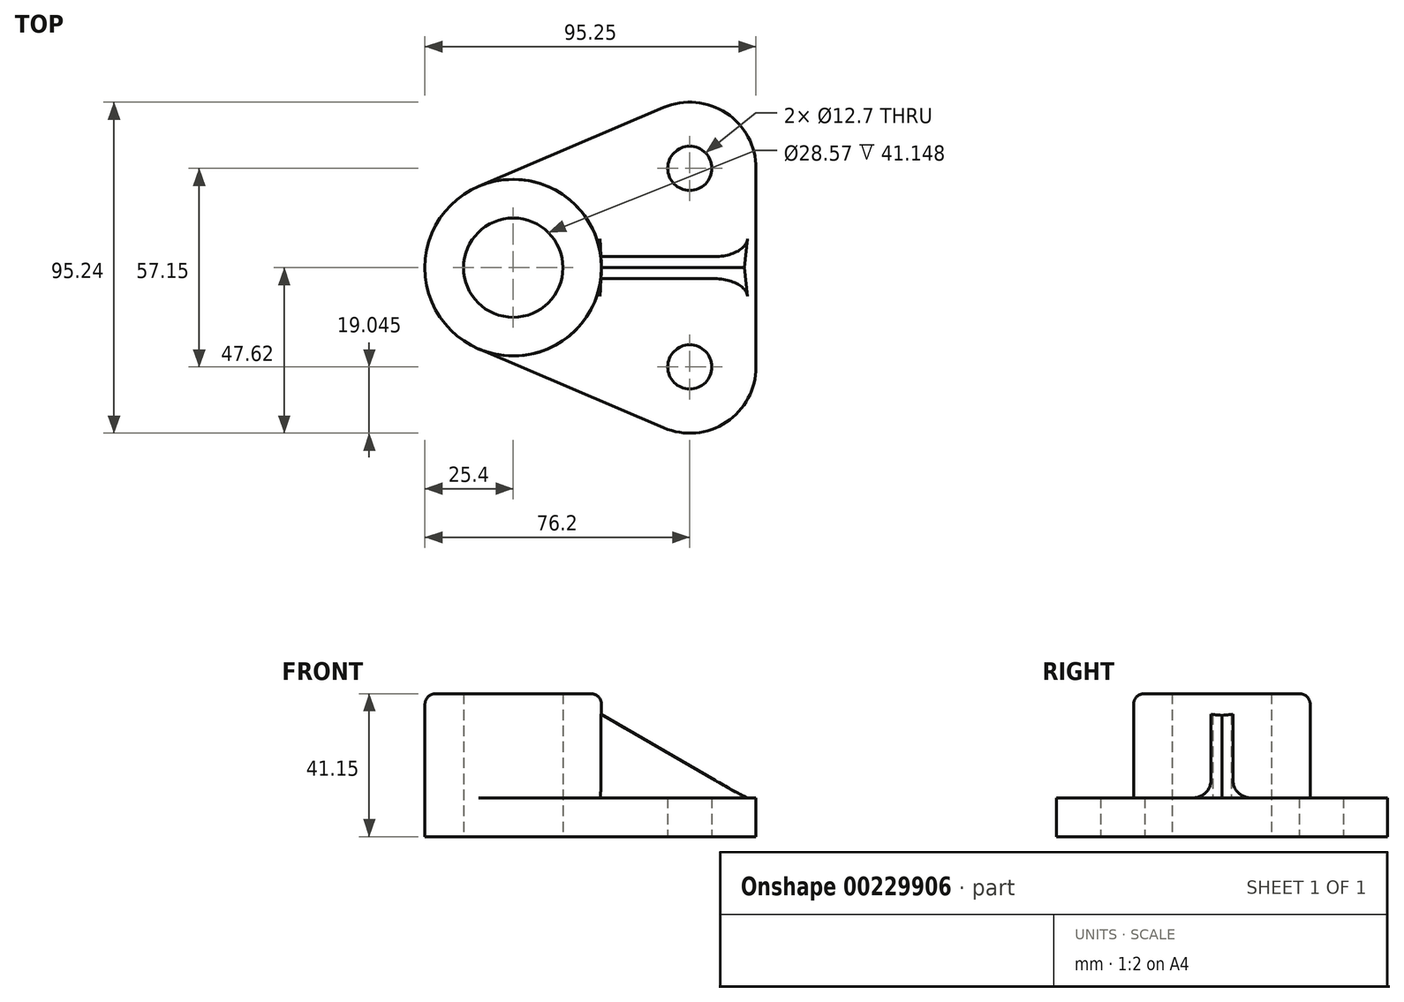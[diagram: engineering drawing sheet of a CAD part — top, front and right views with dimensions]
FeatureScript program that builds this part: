
annotation { "Feature Type Name" : "Feature", "Feature Type Description" : "" }
export const myFeature = defineFeature(function(context is Context, id is Id, definition is map)
    precondition{}
    {
        {
            var Q0;
            Q0=qCreatedBy(makeId("Top.planeOp"),FACE);
            var sketch = newSketch(context, id + "F0", { "sketchPlane" : qUnion([Q0])});
            skCircle(sketch, "E0", {"center": v(0, 0) * mm, "radius": 25.4 * mm});
            skLineSegment(sketch, "E1", {"start": v(0, 0) * mm, "end": v(86.67, 0) * mm, "construction": true});
            skCircle(sketch, "E2", {"center": v(50.8, 28.58) * mm, "radius": 6.35 * mm});
            skCircle(sketch, "E3", {"center": v(50.8, -28.58) * mm, "radius": 6.35 * mm});
            skArc(sketch, "E4", {"start": v(69.85, 28.58) * mm, "mid": v(61.3, 44.47) * mm, "end": v(43.33, 46.1) * mm});
            skArc(sketch, "E5", {"start": v(43.33, -46.1) * mm, "mid": v(61.3, -44.47) * mm, "end": v(69.85, -28.57) * mm});
            skLineSegment(sketch, "E6", {"start": v(43.33, 46.1) * mm, "end": v(-9.97, 23.36) * mm});
            skLineSegment(sketch, "E7", {"start": v(43.33, -46.1) * mm, "end": v(-9.97, -23.36) * mm});
            skLineSegment(sketch, "E8", {"start": v(69.85, 28.58) * mm, "end": v(69.85, -28.57) * mm});
            skCircle(sketch, "E9", {"center": v(0, 0) * mm, "radius": 14.29 * mm});
            skSolve(sketch);
        }
        {
            var Q0;
            Q0=makeQuery(id+"F0.imprint","IMPRINT",FACE,{"disambiguationData":[TD([[makeQuery(id+"F0.imprint","IMPRINT",EDGE,{"derivedFrom":sQuery(id+"F0.wireOp",EDGE,"E2")}),-1.0]])]});
            extrude(context, id + "F1", {"entities" : qUnion([Q0]), "depth" : 11.18 * mm});
        }
        {
            var Q0;
            Q0=makeQuery(id+"F0.imprint","IMPRINT",FACE,{"disambiguationData":[TD([[makeQuery(id+"F0.imprint","IMPRINT",EDGE,{"derivedFrom":sQuery(id+"F0.wireOp",EDGE,"E9")}),-1.0]])]});
            extrude(context, id + "F2", {"entities" : qUnion([Q0]), "operationType" : NewBodyOperationType.ADD, "depth" : 41.15 * mm});
        }
        {
            var Q0;
            Q0=qCreatedBy(makeId("Front.planeOp"),FACE);
            var sketch = newSketch(context, id + "F3", { "sketchPlane" : qUnion([Q0])});
            skLineSegment(sketch, "E10.0", {"start": v(43.33, 11.18) * mm, "end": v(66.55, 11.18) * mm});
            skLineSegment(sketch, "E11", {"start": v(25.4, 34.93) * mm, "end": v(25.4, 11.18) * mm});
            skLineSegment(sketch, "E12", {"start": v(66.55, 11.18) * mm, "end": v(25.4, 34.93) * mm});
            skPoint(sketch, "E13.orphan", {"position": v(69.85, 11.18) * mm});
            skLineSegment(sketch, "E14", {"start": v(25.4, 11.18) * mm, "end": v(43.33, 11.18) * mm});
            skSolve(sketch);
        }
        {
            var Q0;
            Q0=makeQuery(id+"F3.imprint","IMPRINT",FACE,{"disambiguationData":[TD([[makeQuery(id+"F3.imprint","IMPRINT",EDGE,{"derivedFrom":sQuery(id+"F3.wireOp",EDGE,"E10.0")}),1.0]])]});
            extrude(context, id + "F4", {"entities" : qUnion([Q0]), "operationType" : NewBodyOperationType.ADD, "endBound" : BoundingType.SYMMETRIC, "depth" : 6.35 * mm, "hasDraft" : true, "draftAngle" : 3 * degree});
        }
        {
            var Q0;
            Q0=makeQuery(id+"F2.opExtrude","CAP_EDGE",EDGE,{"disambiguationData":[OSD([sQuery(id+"F0.wireOp",EDGE,"E0")])],"isStart":false});
            fillet(context, id + "F5", {"entities" : qUnion([Q0]), "radius" : 3.05 * mm, "tangentPropagation" : true, "allowEdgeOverflow" : false});
        }
        {
            var Q0;
            {var subQ0=sQuery(id+"F0.wireOp",EDGE,"E7");var subQ1=sQuery(id+"F0.wireOp",EDGE,"E0");Q0=makeQuery(id+"F4.boolean.opBoolean","SPLIT",EDGE,{"disambiguationData":[TD([makeQuery(id+"F1.opExtrude","SWEPT_FACE",FACE,{"disambiguationData":[OSD([subQ0])]})])],"derivedFrom":makeQuery(id+"F1.opExtrude","CAP_EDGE",EDGE,{"disambiguationData":[OSD([subQ1])],"isStart":false})});}
            var Q1;
            Q1=makeQuery(id+"F4.boolean.opBoolean","INTERSECT",EDGE,{"derivedFrom":[makeQuery(id+"F1.opExtrude","CAP_FACE",FACE,{"disambiguationData":[OSD([sQuery(id+"F0.wireOp",EDGE,"E0"),sQuery(id+"F0.wireOp",EDGE,"E2"),sQuery(id+"F0.wireOp",EDGE,"E3"),sQuery(id+"F0.wireOp",EDGE,"E4"),sQuery(id+"F0.wireOp",EDGE,"E5"),sQuery(id+"F0.wireOp",EDGE,"E6"),sQuery(id+"F0.wireOp",EDGE,"E7"),sQuery(id+"F0.wireOp",EDGE,"E8")])],"isStart":false}),makeQuery(id+"F4.opExtrude","CAP_FACE",FACE,{"disambiguationData":[OSD([sQuery(id+"F3.wireOp",EDGE,"E10.0"),sQuery(id+"F3.wireOp",EDGE,"E11"),sQuery(id+"F3.wireOp",EDGE,"E12"),sQuery(id+"F3.wireOp",EDGE,"E14")])],"isStart":false})]});
            var Q2;
            {var subQ0=sQuery(id+"F0.wireOp",EDGE,"E6");var subQ1=sQuery(id+"F0.wireOp",EDGE,"E0");Q2=makeQuery(id+"F4.boolean.opBoolean","SPLIT",EDGE,{"disambiguationData":[TD([makeQuery(id+"F1.opExtrude","SWEPT_FACE",FACE,{"disambiguationData":[OSD([subQ0])]})])],"derivedFrom":makeQuery(id+"F1.opExtrude","CAP_EDGE",EDGE,{"disambiguationData":[OSD([subQ1])],"isStart":false})});}
            var Q3;
            Q3=makeQuery(id+"F4.boolean.opBoolean","INTERSECT",EDGE,{"derivedFrom":[makeQuery(id+"F1.opExtrude","CAP_FACE",FACE,{"disambiguationData":[OSD([sQuery(id+"F0.wireOp",EDGE,"E0"),sQuery(id+"F0.wireOp",EDGE,"E2"),sQuery(id+"F0.wireOp",EDGE,"E3"),sQuery(id+"F0.wireOp",EDGE,"E4"),sQuery(id+"F0.wireOp",EDGE,"E5"),sQuery(id+"F0.wireOp",EDGE,"E6"),sQuery(id+"F0.wireOp",EDGE,"E7"),sQuery(id+"F0.wireOp",EDGE,"E8")])],"isStart":false}),makeQuery(id+"F4.opExtrude","CAP_FACE",FACE,{"disambiguationData":[OSD([sQuery(id+"F3.wireOp",EDGE,"E10.0"),sQuery(id+"F3.wireOp",EDGE,"E11"),sQuery(id+"F3.wireOp",EDGE,"E12"),sQuery(id+"F3.wireOp",EDGE,"E14")])],"isStart":true})]});
            fillet(context, id + "F6", {"entities" : qUnion([Q0, Q1, Q2, Q3]), "radius" : 5.08 * mm, "tangentPropagation" : true, "allowEdgeOverflow" : false});
        }
    });
